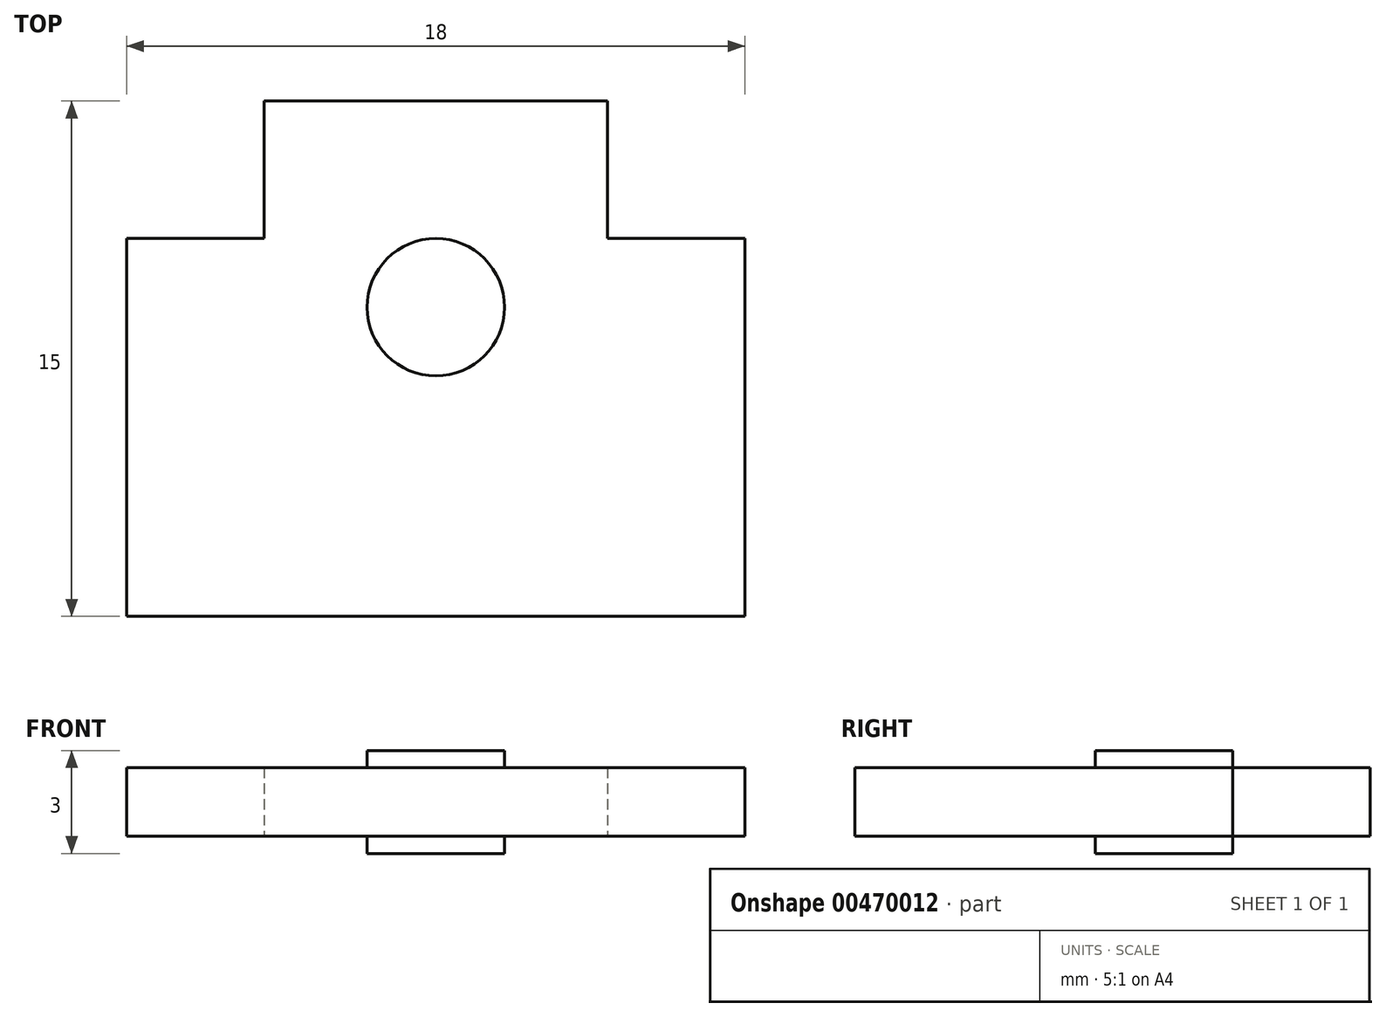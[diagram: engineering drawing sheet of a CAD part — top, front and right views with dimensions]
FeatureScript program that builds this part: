
annotation { "Feature Type Name" : "Feature", "Feature Type Description" : "" }
export const myFeature = defineFeature(function(context is Context, id is Id, definition is map)
    precondition{}
    {
        {
            var Q0;
            Q0=qCreatedBy(makeId("Top.planeOp"),FACE);
            var sketch = newSketch(context, id + "F0", { "sketchPlane" : qUnion([Q0])});
            skCircle(sketch, "E0", {"center": v(0, 0) * mm, "radius": 2 * mm});
            skLineSegment(sketch, "E1.bottom", {"start": v(9, -9) * mm, "end": v(-9, -9) * mm});
            skLineSegment(sketch, "E1.top", {"start": v(9, 9) * mm, "end": v(-9, 9) * mm});
            skLineSegment(sketch, "E1.left", {"start": v(9, -9) * mm, "end": v(9, 9) * mm});
            skLineSegment(sketch, "E1.right", {"start": v(-9, -9) * mm, "end": v(-9, 9) * mm});
            skLineSegment(sketch, "E2", {"start": v(-9, 6) * mm, "end": v(9, 6) * mm});
            skLineSegment(sketch, "E3.bottom", {"start": v(-9, 6) * mm, "end": v(-5, 6) * mm});
            skLineSegment(sketch, "E3.top", {"start": v(-9, 2) * mm, "end": v(-5, 2) * mm});
            skLineSegment(sketch, "E3.left", {"start": v(-9, 6) * mm, "end": v(-9, 2) * mm});
            skLineSegment(sketch, "E3.right", {"start": v(-5, 6) * mm, "end": v(-5, 2) * mm});
            skLineSegment(sketch, "E4.bottom", {"start": v(9, 6) * mm, "end": v(5, 6) * mm});
            skLineSegment(sketch, "E4.top", {"start": v(9, 2) * mm, "end": v(5, 2) * mm});
            skLineSegment(sketch, "E4.left", {"start": v(9, 6) * mm, "end": v(9, 2) * mm});
            skLineSegment(sketch, "E4.right", {"start": v(5, 6) * mm, "end": v(5, 2) * mm});
            skSolve(sketch);
        }
        {
            var Q0;
            Q0=makeQuery(id+"F0.imprint","IMPRINT",FACE,{"disambiguationData":[TD([[makeQuery(id+"F0.imprint","IMPRINT",EDGE,{"derivedFrom":sQuery(id+"F0.wireOp",EDGE,"E0")}),-1.0]])]});
            extrude(context, id + "F1", {"entities" : qUnion([Q0]), "endBound" : BoundingType.SYMMETRIC, "depth" : 2 * mm, "offsetDistance" : 25 * mm});
        }
        {
            var Q0;
            Q0=makeQuery(id+"F0.imprint","IMPRINT",FACE,{"disambiguationData":[TD([[makeQuery(id+"F0.imprint","IMPRINT",EDGE,{"derivedFrom":sQuery(id+"F0.wireOp",EDGE,"E0")}),1.0]])]});
            extrude(context, id + "F2", {"entities" : qUnion([Q0]), "operationType" : NewBodyOperationType.ADD, "endBound" : BoundingType.SYMMETRIC, "depth" : 3 * mm, "offsetDistance" : 25 * mm});
        }
    });
